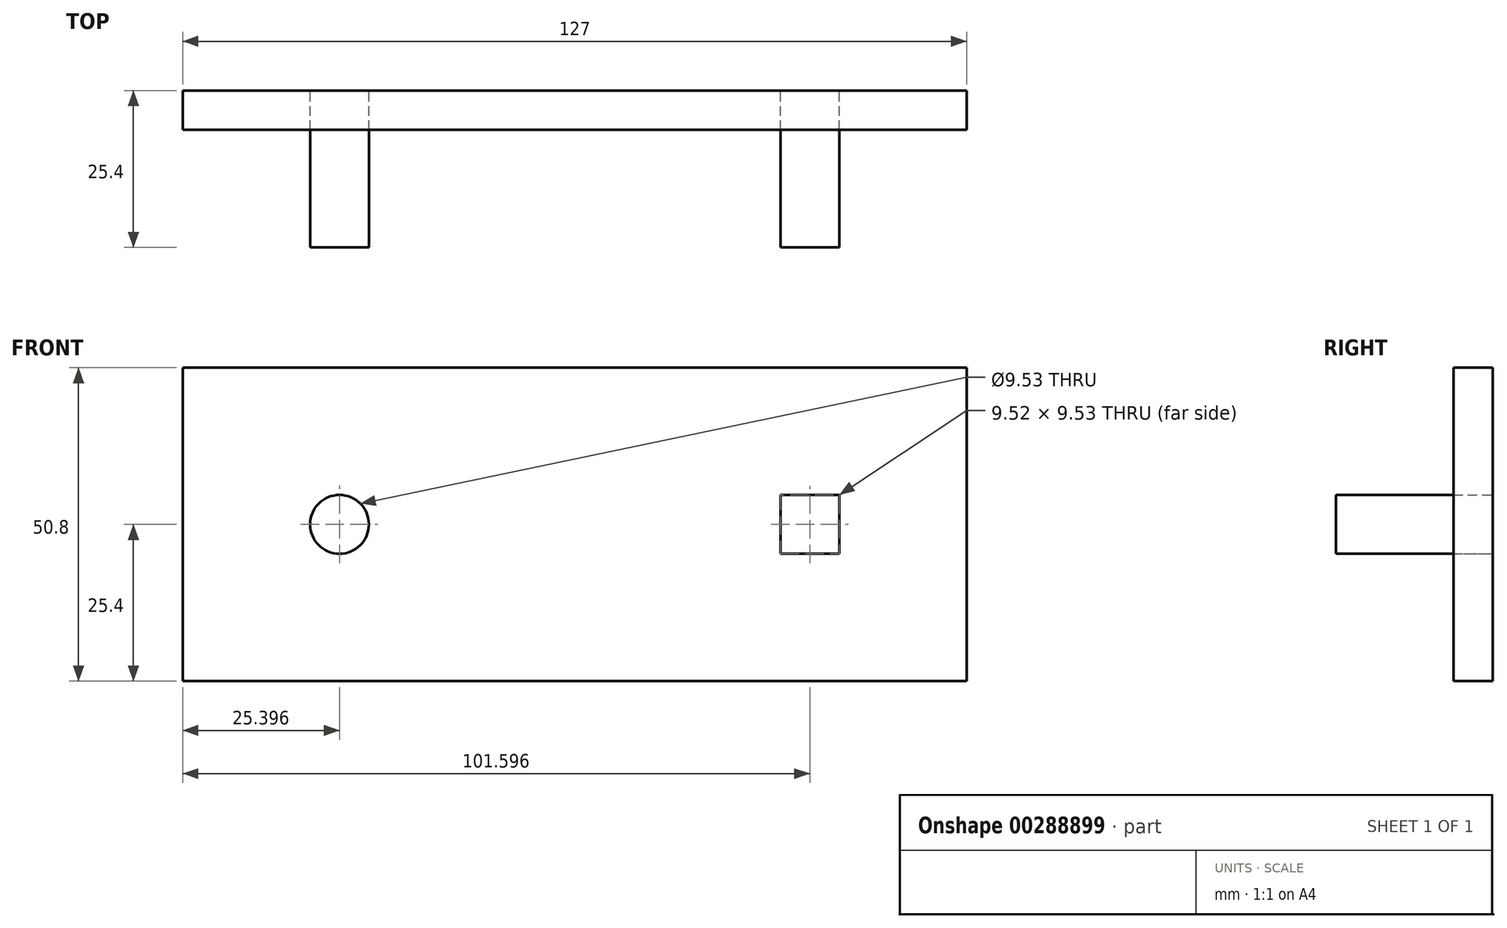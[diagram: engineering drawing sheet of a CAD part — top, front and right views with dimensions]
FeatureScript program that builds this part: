
annotation { "Feature Type Name" : "Feature", "Feature Type Description" : "" }
export const myFeature = defineFeature(function(context is Context, id is Id, definition is map)
    precondition{}
    {
        {
            var Q0;
            Q0=qCreatedBy(makeId("Front.planeOp"),FACE);
            var sketch = newSketch(context, id + "F0", { "sketchPlane" : qUnion([Q0])});
            skLineSegment(sketch, "E0.bottom", {"start": v(-46.92, 25.4) * mm, "end": v(80.08, 25.4) * mm});
            skLineSegment(sketch, "E0.top", {"start": v(-46.92, -25.4) * mm, "end": v(80.08, -25.4) * mm});
            skLineSegment(sketch, "E0.left", {"start": v(-46.92, 25.4) * mm, "end": v(-46.92, -25.4) * mm});
            skLineSegment(sketch, "E0.right", {"start": v(80.08, 25.4) * mm, "end": v(80.08, -25.4) * mm});
            skCircle(sketch, "E1", {"center": v(-21.52, 0) * mm, "radius": 4.76 * mm});
            skLineSegment(sketch, "E2.bottom", {"start": v(49.91, 4.76) * mm, "end": v(59.44, 4.76) * mm});
            skLineSegment(sketch, "E2.top", {"start": v(49.91, -4.76) * mm, "end": v(59.44, -4.76) * mm});
            skLineSegment(sketch, "E2.left", {"start": v(49.91, 4.76) * mm, "end": v(49.91, -4.76) * mm});
            skLineSegment(sketch, "E2.right", {"start": v(59.44, 4.76) * mm, "end": v(59.44, -4.76) * mm});
            skSolve(sketch);
        }
        {
            var Q0;
            Q0=makeQuery(id+"F0.imprint","IMPRINT",FACE,{"disambiguationData":[TD([[makeQuery(id+"F0.imprint","IMPRINT",EDGE,{"derivedFrom":sQuery(id+"F0.wireOp",EDGE,"E1")}),1.0]])]});
            var Q1;
            Q1=makeQuery(id+"F0.imprint","IMPRINT",FACE,{"disambiguationData":[TD([[makeQuery(id+"F0.imprint","IMPRINT",EDGE,{"derivedFrom":sQuery(id+"F0.wireOp",EDGE,"E2.bottom")}),-1.0]])]});
            extrude(context, id + "F1", {"entities" : qUnion([Q0, Q1]), "depth" : 25.4 * mm});
        }
        {
            var Q0;
            Q0=makeQuery(id+"F0.imprint","IMPRINT",FACE,{"disambiguationData":[TD([[makeQuery(id+"F0.imprint","IMPRINT",EDGE,{"derivedFrom":sQuery(id+"F0.wireOp",EDGE,"E0.bottom")}),-1.0]])]});
            extrude(context, id + "F2", {"entities" : qUnion([Q0]), "depth" : 6.35 * mm});
        }
    });
